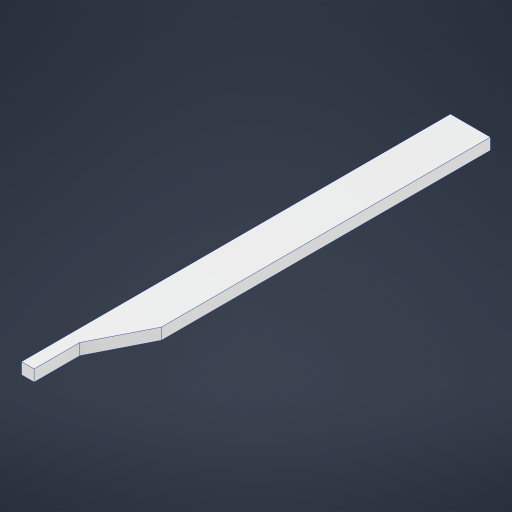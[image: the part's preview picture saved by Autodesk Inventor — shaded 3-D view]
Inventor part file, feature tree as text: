
AUTODESK INVENTOR PART (.ipt)
format: ipt  version: 2024 (Build 280153000, 153)  size: 257,024 bytes
history: native  units: mm
features: extrude x3, sketch x3
ambient origin geometry x8: Origin, YZ Plane, XZ Plane, XY Plane, X Axis, Y Axis, Z Axis, Center Point
bodies: Solid1 (feature_tree)
feature tree (6):
  extrude  "Extrusion1"  Depth=750.0mm
  extrude  "Extrusion2"  Depth=20.0mm TaperAngle=0.0deg
  extrude  "Extrusion3"  Depth=22.0mm TaperAngle=0.0deg
  sketch  "Sketch1"  dims[d0=750.0mm d1=90.0mm]
  sketch  "Sketch2"  dims[d2=20.0mm d3=0.0mm d4=25.0mm d5=0.0mm]
  sketch  "Sketch3"  dims[d7=70.0mm d8=30.0mm d9=0.0mm d10=0.0mm d11=80.0mm d13=82.0mm d14=82.0mm d15=162.0mm d16=162.0mm d17=9.0mm d18=0.0mm d19=22.0mm d20=0.0mm]
